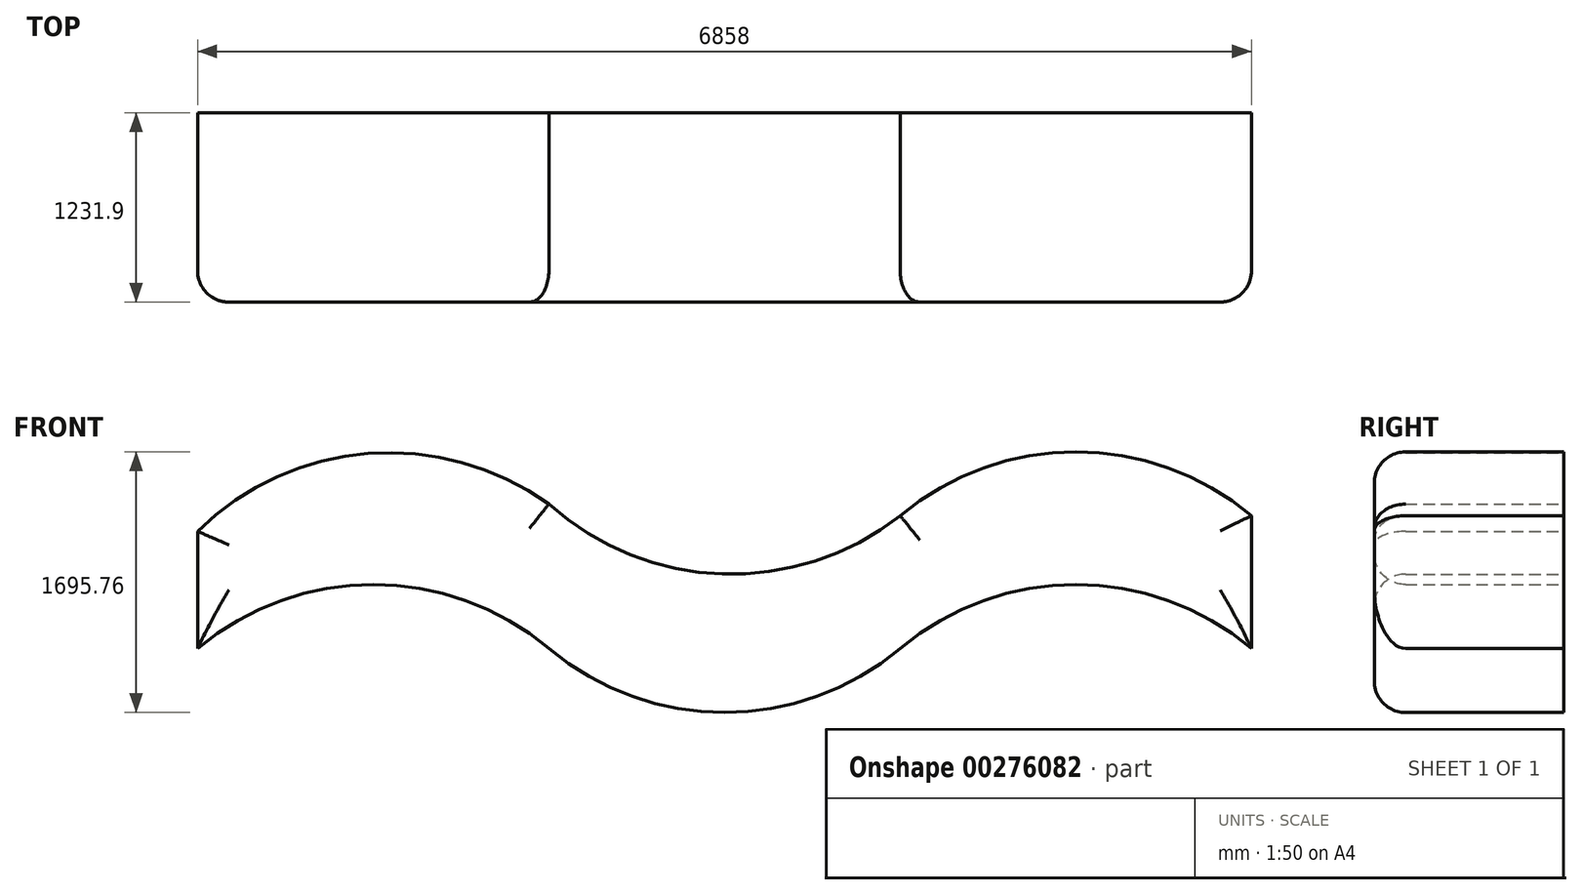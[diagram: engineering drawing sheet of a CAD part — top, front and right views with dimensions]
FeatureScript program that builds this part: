
annotation { "Feature Type Name" : "Feature", "Feature Type Description" : "" }
export const myFeature = defineFeature(function(context is Context, id is Id, definition is map)
    precondition{}
    {
        {
            var Q0;
            Q0=qCreatedBy(makeId("Front.planeOp"),FACE);
            var sketch = newSketch(context, id + "F0", { "sketchPlane" : qUnion([Q0])});
            skLineSegment(sketch, "E0", {"start": v(0, 0) * mm, "end": v(2286, 0) * mm});
            skLineSegment(sketch, "E1", {"start": v(2286, 0) * mm, "end": v(0, 0) * mm});
            skLineSegment(sketch, "E2", {"start": v(-2286, 0) * mm, "end": v(0, 0) * mm});
            skLineSegment(sketch, "E3", {"start": v(-2286, 0) * mm, "end": v(-4572, 0) * mm});
            skLineSegment(sketch, "E4", {"start": v(-4572, 0) * mm, "end": v(-4572, 762) * mm});
            skLineSegment(sketch, "E5", {"start": v(-2286, 0) * mm, "end": v(-2286, 939.8) * mm});
            skLineSegment(sketch, "E6", {"start": v(0, 0) * mm, "end": v(0, 863.6) * mm});
            skLineSegment(sketch, "E7", {"start": v(2286, 0) * mm, "end": v(2286, 863.6) * mm});
            skArc(sketch, "E8", {"start": v(-2286, 939.8) * mm, "mid": v(-3461.49, 1268.62) * mm, "end": v(-4572, 762) * mm});
            skArc(sketch, "E9", {"start": v(-2286, 0) * mm, "mid": v(-3429, 416.08) * mm, "end": v(-4572, 0) * mm});
            skArc(sketch, "E10", {"start": v(-2286, 0) * mm, "mid": v(-1143, -416.08) * mm, "end": v(0, 0) * mm});
            skArc(sketch, "E11", {"start": v(-2286, 939.8) * mm, "mid": v(-1156.88, 485.32) * mm, "end": v(0, 863.6) * mm});
            skArc(sketch, "E12", {"start": v(2286, 863.6) * mm, "mid": v(1143, 1279.68) * mm, "end": v(0, 863.6) * mm});
            skArc(sketch, "E13", {"start": v(2286, 0) * mm, "mid": v(1143, 416.08) * mm, "end": v(0, 0) * mm});
            skSolve(sketch);
        }
        {
            var Q0;
            Q0=makeQuery(id+"F0.imprint","IMPRINT",FACE,{"disambiguationData":[TD([[makeQuery(id+"F0.imprint","IMPRINT",EDGE,{"derivedFrom":sQuery(id+"F0.wireOp",EDGE,"E4")}),-1.0]])]});
            var Q1;
            Q1=makeQuery(id+"F0.imprint","IMPRINT",FACE,{"disambiguationData":[TD([[makeQuery(id+"F0.imprint","IMPRINT",EDGE,{"derivedFrom":sQuery(id+"F0.wireOp",EDGE,"E2")}),1.0]])]});
            var Q2;
            Q2=makeQuery(id+"F0.imprint","IMPRINT",FACE,{"disambiguationData":[TD([[makeQuery(id+"F0.imprint","IMPRINT",EDGE,{"derivedFrom":sQuery(id+"F0.wireOp",EDGE,"E2")}),-1.0]])]});
            var Q3;
            Q3=makeQuery(id+"F0.imprint","IMPRINT",FACE,{"disambiguationData":[TD([[makeQuery(id+"F0.imprint","IMPRINT",EDGE,{"derivedFrom":sQuery(id+"F0.wireOp",EDGE,"E6")}),-1.0]])]});
            extrude(context, id + "F1", {"entities" : qUnion([Q0, Q1, Q2, Q3]), "depth" : 1231.9 * mm});
        }
        {
            var Q0;
            Q0=makeQuery(id+"F1.opExtrude","CAP_EDGE",EDGE,{"disambiguationData":[OSD([sQuery(id+"F0.wireOp",EDGE,"E4")])],"isStart":false});
            var Q1;
            Q1=makeQuery(id+"F1.opExtrude","CAP_EDGE",EDGE,{"disambiguationData":[OSD([sQuery(id+"F0.wireOp",EDGE,"E8")])],"isStart":false});
            var Q2;
            Q2=makeQuery(id+"F1.opExtrude","CAP_EDGE",EDGE,{"disambiguationData":[OSD([sQuery(id+"F0.wireOp",EDGE,"E9")])],"isStart":false});
            var Q3;
            Q3=makeQuery(id+"F1.opExtrude","CAP_EDGE",EDGE,{"disambiguationData":[OSD([sQuery(id+"F0.wireOp",EDGE,"E10")])],"isStart":false});
            var Q4;
            Q4=makeQuery(id+"F1.opExtrude","CAP_EDGE",EDGE,{"disambiguationData":[OSD([sQuery(id+"F0.wireOp",EDGE,"E11")])],"isStart":false});
            var Q5;
            Q5=makeQuery(id+"F1.opExtrude","CAP_EDGE",EDGE,{"disambiguationData":[OSD([sQuery(id+"F0.wireOp",EDGE,"E12")])],"isStart":false});
            var Q6;
            Q6=makeQuery(id+"F1.opExtrude","CAP_EDGE",EDGE,{"disambiguationData":[OSD([sQuery(id+"F0.wireOp",EDGE,"E13")])],"isStart":false});
            var Q7;
            Q7=makeQuery(id+"F1.opExtrude","CAP_EDGE",EDGE,{"disambiguationData":[OSD([sQuery(id+"F0.wireOp",EDGE,"E7")])],"isStart":false});
            fillet(context, id + "F2", {"entities" : qUnion([Q0, Q1, Q2, Q3, Q4, Q5, Q6, Q7]), "radius" : 203.2 * mm, "tangentPropagation" : true, "allowEdgeOverflow" : false});
        }
    });
